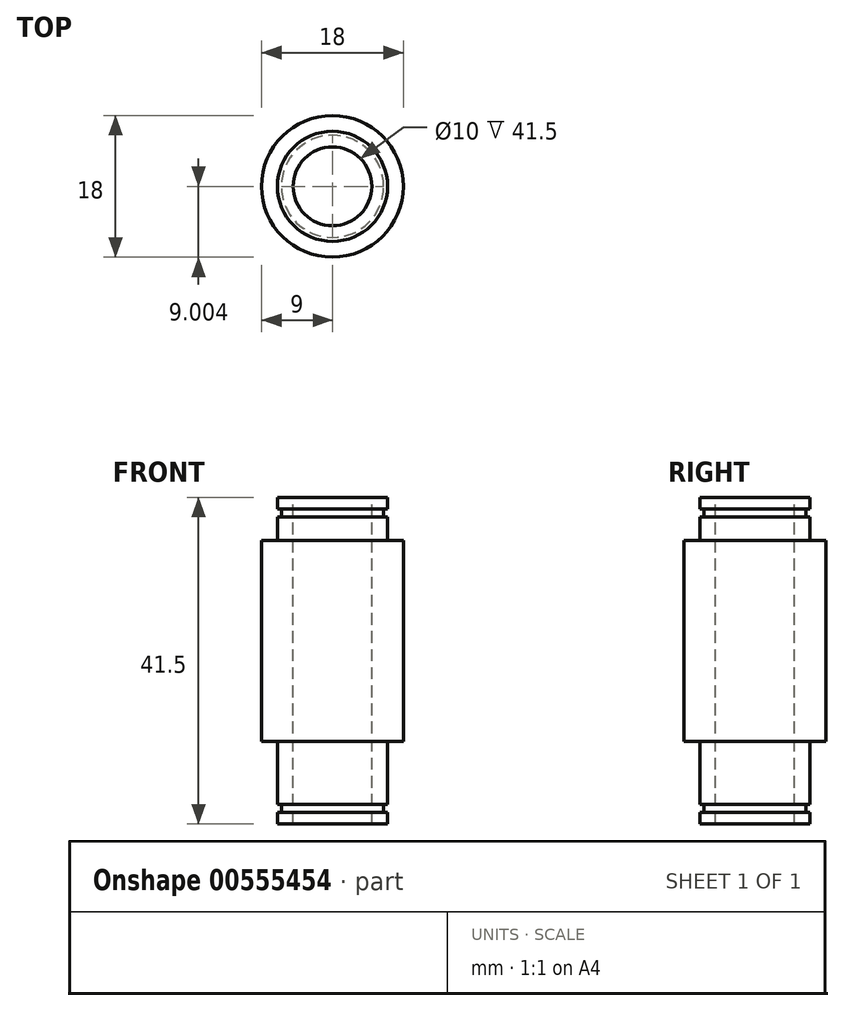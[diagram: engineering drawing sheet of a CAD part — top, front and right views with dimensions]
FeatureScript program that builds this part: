
annotation { "Feature Type Name" : "Feature", "Feature Type Description" : "" }
export const myFeature = defineFeature(function(context is Context, id is Id, definition is map)
    precondition{}
    {
        {
            var Q0;
            Q0=qCreatedBy(makeId("Right.planeOp"),FACE);
            var sketch = newSketch(context, id + "F0", { "sketchPlane" : qUnion([Q0])});
            skLineSegment(sketch, "E0", {"start": v(-42.52, 30.41) * mm, "end": v(-42.52, -11.09) * mm});
            skLineSegment(sketch, "E1", {"start": v(-42.52, -11.09) * mm, "end": v(-44.52, -11.09) * mm});
            skLineSegment(sketch, "E2", {"start": v(-44.52, -11.09) * mm, "end": v(-44.52, -9.59) * mm});
            skLineSegment(sketch, "E3", {"start": v(-44.52, -9.59) * mm, "end": v(-44.02, -9.59) * mm});
            skLineSegment(sketch, "E4", {"start": v(-44.02, -9.59) * mm, "end": v(-44.02, -8.59) * mm});
            skLineSegment(sketch, "E5", {"start": v(-44.02, -8.59) * mm, "end": v(-44.52, -8.59) * mm});
            skLineSegment(sketch, "E6", {"start": v(-44.52, -8.59) * mm, "end": v(-44.52, -0.59) * mm});
            skLineSegment(sketch, "E7", {"start": v(-44.52, -0.59) * mm, "end": v(-46.52, -0.59) * mm});
            skLineSegment(sketch, "E8", {"start": v(-46.52, -0.59) * mm, "end": v(-46.52, 24.91) * mm});
            skLineSegment(sketch, "E9", {"start": v(-46.52, 24.91) * mm, "end": v(-44.52, 24.91) * mm});
            skLineSegment(sketch, "E10", {"start": v(-44.52, 28.91) * mm, "end": v(-44.02, 28.91) * mm});
            skLineSegment(sketch, "E11", {"start": v(-44.52, 30.41) * mm, "end": v(-42.52, 30.41) * mm});
            skLineSegment(sketch, "E12", {"start": v(-37.52, 30.41) * mm, "end": v(-37.52, -11.09) * mm});
            skLineSegment(sketch, "E13", {"start": v(-44.52, 30.41) * mm, "end": v(-44.52, 28.91) * mm});
            skLineSegment(sketch, "E14", {"start": v(-44.02, 28.91) * mm, "end": v(-44.02, 27.91) * mm});
            skLineSegment(sketch, "E15", {"start": v(-44.02, 27.91) * mm, "end": v(-44.52, 27.91) * mm});
            skLineSegment(sketch, "E16", {"start": v(-44.52, 27.91) * mm, "end": v(-44.52, 24.91) * mm});
            skSolve(sketch);
        }
        {
            var Q0;
            Q0=makeQuery(id+"F0.imprint","IMPRINT",FACE,{"disambiguationData":[TD([[makeQuery(id+"F0.imprint","IMPRINT",EDGE,{"derivedFrom":sQuery(id+"F0.wireOp",EDGE,"E0")}),-1.0]])]});
            var Q1;
            Q1=sQuery(id+"F0.wireOp",EDGE,"E12");
            revolve(context, id + "F1", {"surfaceOperationType" : NewSurfaceOperationType.NEW, "entities" : qUnion([Q0]), "axis" : qUnion([Q1]), "revolveType" : RevolveType.FULL});
        }
    });
